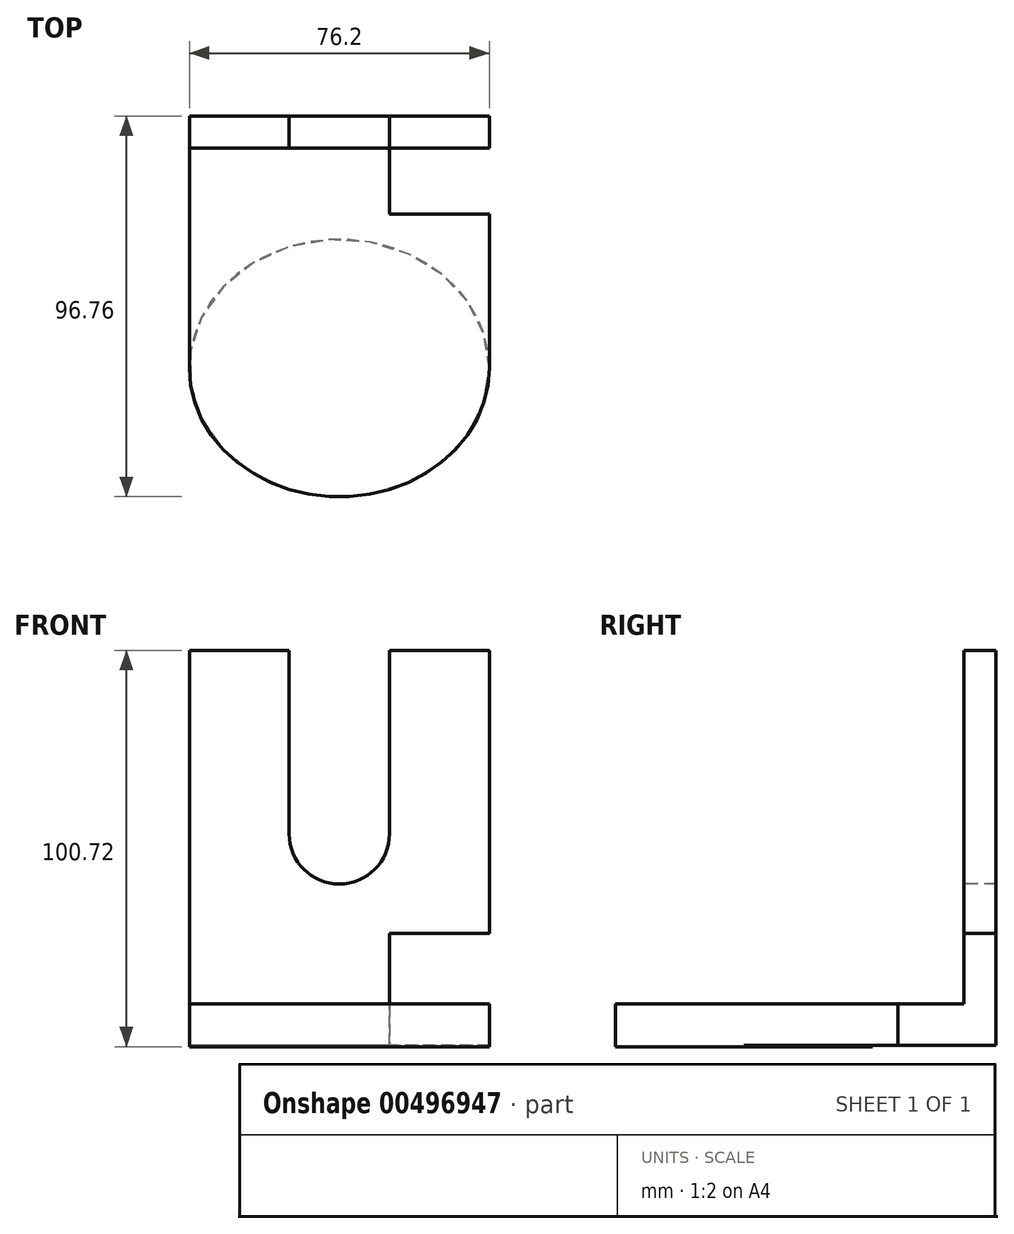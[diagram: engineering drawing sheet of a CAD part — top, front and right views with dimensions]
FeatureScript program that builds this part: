
annotation { "Feature Type Name" : "Feature", "Feature Type Description" : "" }
export const myFeature = defineFeature(function(context is Context, id is Id, definition is map)
    precondition{}
    {
        {
            var Q0;
            Q0=qCreatedBy(makeId("Right.planeOp"),FACE);
            var sketch = newSketch(context, id + "F0", { "sketchPlane" : qUnion([Q0])});
            skLineSegment(sketch, "E0", {"start": v(22.1, 69.66) * mm, "end": v(22.1, -30.77) * mm});
            skLineSegment(sketch, "E1", {"start": v(22.1, -30.77) * mm, "end": v(-41.96, -30.77) * mm});
            skLineSegment(sketch, "E2", {"start": v(-41.96, -30.77) * mm, "end": v(-41.96, -20.14) * mm});
            skLineSegment(sketch, "E3", {"start": v(-41.96, -20.14) * mm, "end": v(13.99, -20.14) * mm});
            skLineSegment(sketch, "E4", {"start": v(13.99, -20.14) * mm, "end": v(13.99, 69.66) * mm});
            skLineSegment(sketch, "E5", {"start": v(13.99, 69.66) * mm, "end": v(22.1, 69.66) * mm});
            skSolve(sketch);
        }
        {
            var Q0;
            Q0 = qSketchRegion(id + "F0", true);
            extrude(context, id + "F1", {"entities" : qUnion([Q0]), "depth" : 76.2 * mm, "symmetric" : true});
        }
        {
            var Q0;
            Q0=makeQuery(id+"F1.opExtrude","SWEPT_FACE",FACE,{"disambiguationData":[OSD([sQuery(id+"F0.wireOp",EDGE,"E4")])]});
            var sketch = newSketch(context, id + "F2", { "sketchPlane" : qUnion([Q0])});
            skLineSegment(sketch, "E6.bottom", {"start": v(12.74, 69.66) * mm, "end": v(-12.74, 69.66) * mm});
            skLineSegment(sketch, "E6.top", {"start": v(12.74, 23) * mm, "end": v(-12.74, 23) * mm});
            skLineSegment(sketch, "E6.left", {"start": v(12.74, 69.66) * mm, "end": v(12.74, 23) * mm});
            skLineSegment(sketch, "E6.right", {"start": v(-12.74, 69.66) * mm, "end": v(-12.74, 23) * mm});
            skPoint(sketch, "E6.middle", {"position": v(0, 46.33) * mm});
            skSolve(sketch);
        }
        {
            var Q0;
            Q0 = qSketchRegion(id + "F2", true);
            extrude(context, id + "F3", {"entities" : qUnion([Q0]), "operationType" : NewBodyOperationType.REMOVE, "oppositeDirection" : true, "depth" : 25.4 * mm});
        }
        {
            var Q0;
            Q0=makeQuery(id+"F1.opExtrude","SWEPT_FACE",FACE,{"disambiguationData":[OSD([sQuery(id+"F0.wireOp",EDGE,"E4")])]});
            var sketch = newSketch(context, id + "F4", { "sketchPlane" : qUnion([Q0])});
            skCircle(sketch, "E7", {"center": v(0, 23) * mm, "radius": 12.74 * mm});
            skSolve(sketch);
        }
        {
            var Q0;
            Q0 = qSketchRegion(id + "F4", true);
            extrude(context, id + "F5", {"entities" : qUnion([Q0]), "operationType" : NewBodyOperationType.REMOVE, "oppositeDirection" : true, "depth" : 25.4 * mm});
        }
        {
            var Q0;
            Q0=makeQuery(id+"F1.opExtrude","SWEPT_FACE",FACE,{"disambiguationData":[OSD([sQuery(id+"F0.wireOp",EDGE,"E3")])]});
            var sketch = newSketch(context, id + "F6", { "sketchPlane" : qUnion([Q0])});
            skEllipse(sketch, "E8", {"center": v(0, -41.96) * mm, "majorRadius": 38.1 * mm, "minorRadius": 32.69 * mm, "majorAxis": v(1, 0)});
            skSolve(sketch);
        }
        {
            var Q0;
            Q0 = qSketchRegion(id + "F6", true);
            extrude(context, id + "F7", {"entities" : qUnion([Q0]), "operationType" : NewBodyOperationType.ADD, "oppositeDirection" : true, "depth" : 10.92 * mm});
        }
        {
            var Q0;
            Q0=makeQuery(id+"F1.opExtrude","CAP_FACE",FACE,{"disambiguationData":[OSD([sQuery(id+"F0.wireOp",EDGE,"E0"),sQuery(id+"F0.wireOp",EDGE,"E1"),sQuery(id+"F0.wireOp",EDGE,"E2"),sQuery(id+"F0.wireOp",EDGE,"E3"),sQuery(id+"F0.wireOp",EDGE,"E4"),sQuery(id+"F0.wireOp",EDGE,"E5")])],"isStart":false});
            var sketch = newSketch(context, id + "F8", { "sketchPlane" : qUnion([Q0])});
            skLineSegment(sketch, "E9.bottom", {"start": v(-2.8, -33.57) * mm, "end": v(28.81, -33.57) * mm});
            skLineSegment(sketch, "E9.top", {"start": v(-2.8, -2.24) * mm, "end": v(28.81, -2.24) * mm});
            skLineSegment(sketch, "E9.left", {"start": v(-2.8, -33.57) * mm, "end": v(-2.8, -2.24) * mm});
            skLineSegment(sketch, "E9.right", {"start": v(28.81, -33.57) * mm, "end": v(28.81, -2.24) * mm});
            skSolve(sketch);
        }
        {
            var Q0;
            Q0 = qSketchRegion(id + "F8", true);
            extrude(context, id + "F9", {"entities" : qUnion([Q0]), "operationType" : NewBodyOperationType.REMOVE, "oppositeDirection" : true, "depth" : 25.4 * mm});
        }
    });
